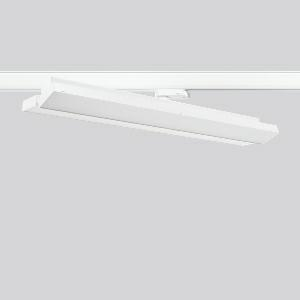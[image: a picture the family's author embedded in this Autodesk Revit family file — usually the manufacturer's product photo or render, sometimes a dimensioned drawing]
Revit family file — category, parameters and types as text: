
# Revit family: tx-move_742164_002_2_76_0ea8
name_source: partatom
category: Lighting Fixtures
units: mm (PartAtom-declared; Revit-internal decimal feet)

## family parameters
Cut with Voids When Loaded = No
Host = Face
Light Source = No
Part Type = Normal
Room Calculation Point = No
Round Connector Dimension = Use Diameter
Shared = No

## types (1)
- MultiLumen 1 (1 x LED Modul 927, 1775 lm, 2700)
    Apparent Load = 38 VA
    CIE Flux Codes = 47 79 96 100 100
    Color Rendering = 92
    Color Temperature = 2700
    Default Elevation = 1800 mm
    Description = Series: TX-MOVE
Multifunctional surface-mounted spotlight for area lighting. Very flat design. Housing: sheet steel, powder-coated. Rotation range: 356°. Swivel range: 90°. Consistent alignment possible with visible tilt scale. High-efficiency LED units with flush-mounted opal diffuser made of non-yellowing PMMA. Symmetrical wide beam light distribution. Best colour rendering with CRI >90 for fresh products and coloured textiles. With adapter for RZB 3-circuit DALI tracks. Suitable for Track on ceiling. MultiLumen: Luminous flux adjustable in 3 steps. Factory setting is the highest luminous flux. Environmentally friendly and resource-saving due to replaceable and recyclable components. 
Colour: traffic white, matt (RAL 9016)
Length: 570 mm
Width: 119 mm
Height: 88 mm
Lamp: LED
Socket: without socket
Colour temperature: 2700K
Colour rendering index (CRI): 90
System power: 38 W
Rated luminous flux: 3550 lm
Luminous efficiency: 93 lm/W
System power 2: 51 W
Rated luminous flux 2: 4650 lm
Luminous efficiency 2: 91 lm/W
System power 3: 62 W
Rated luminous flux 3: 5500 lm
Luminous efficiency 3: 89 lm/W
Control gear: Dimmable EVG, DALI
Protection class: I
Type of protection: IP 20
    Height = 75 mm
    Lamp = 1 x LED Modul 927
    Lamp Light Flux = 1775 lm
    Lamp count = 1
    Length = 569 mm
    Lifetime = 50000 h
    Luminous efficacy = 93 lm/W
    Manufacturer = RZB
    ModVariant = No
    Model = 742164.002.2.76
    Mounting Place = Ceiling
    Mounting Type = Surface mounted
    Number of Poles = 1
    OnlyDefault = Yes
    Power Factor = 1
    Product Name = TX-MOVE
    Product group = Track mounted projectors
    ProductGroupID = 301
    Protection Class = Protection class I
    Protection Degree = IP 20
    RLX_Detail_Level = 1
    RLX_Emergency_Light_Flux = 0 lm
    RLX_Emergency_Type = 0
    RLX_Emergency_Type_DB = No
    RlxData = <blob elided: 29945 chars, md5=801597c3>
    Socket = socket
    Standby Power = 0 W
    System Light Flux = 3550 lm
    System Power = 38 W
    Type Comments = MultiLumen 1
    Type Image = 742164.002.jpg
    URL = http://relux.com
    VarID = multilumen_1
    Voltage = 0 V
    Weight = 0.00 kg
    Width = 119 mm

## geometry (parser evidence)
native form markers: Blend x4, Sweep x13
no freeform markers — native parametric forms only
